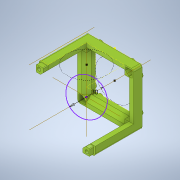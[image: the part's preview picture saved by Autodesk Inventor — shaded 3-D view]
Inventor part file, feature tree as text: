
AUTODESK INVENTOR PART (.ipt)
format: ipt  version: 2022 (Build 260153000, 153)  size: 558,080 bytes
history: native  units: mm
features: projected_geometry x16, sketch x13, extrude x11, plane x7, other x5, hole x3, fillet x2
ambient origin geometry x8: Origin, YZ Plane, XZ Plane, XY Plane, X Axis, Y Axis, Z Axis, Center Point
bodies: Solid1 (feature_tree)
feature tree (57):
  extrude  "Extrusion1"  Depth=49.7mm
  extrude  "Extrusion2"  Depth=8.0mm TaperAngle=0.0deg
  hole  "Hole1"  [1 undecoded]
  sketch  "Sketch4"  dims[d8=3.1mm d9=6.0mm d10=5.5mm d11=4.6mm d12=90.0deg d13=16.0mm d14=20.594885mm d23=2.0mm d30=33.8mm d31=0.0mm]
  sketch  "Sketch5"  dims[d35=33.8mm d36=0.0mm d39=53.8mm]
  other  "Work Axis1"
  other  "Work Axis2"
  fillet  "Fillet1"  Radius=33.8mm
  extrude  "Extrusion3"  Depth=53.8mm
  extrude  "Extrusion4"  Depth=2.0mm
  plane  "Work Plane1"
  extrude  "Extrusion5"  Depth=3.65mm
  hole  "Hole2"  [1 undecoded]
  extrude  "Extrusion6"  Depth=3.65mm
  extrude  "Extrusion7"  Depth=3.78mm
  extrude  "Extrusion8"  Depth=3.78mm
  fillet  "Fillet2"  Radius=3.78mm
  extrude  "Extrusion9"  Depth=10.0mm TaperAngle=0.0deg
  extrude  "Extrusion10"  Depth=3.7mm TaperAngle=0.0deg
  plane  "Work Plane2"
  plane  "Work Plane3"
  hole  "Hole9"  [1 undecoded]
  extrude  "Extrusion11"  Depth=2.0mm
  other  "Work Axis18"
  plane  "Work Plane4"
  sketch  "Sketch23"  dims[d112=45.0deg d120=10.0mm d121=0.0mm d124=3.7mm d125=0.0mm d130=4.2mm d131=0.0mm d132=2.0mm d133=0.5mm d134=3.4mm d135=21.0mm d136=7.38mm d137=3.69mm d138=40.0mm d140=360.0deg d142=4.0mm d143=0.0mm d144=4.95mm d145=2.05mm d146=5.5mm d147=40.0mm d149=360.0deg d151=2.2mm d152=0.0mm d153=3.1mm d154=6.0mm d155=5.5mm d156=3.2mm d157=90.0deg d158=16.0mm d159=20.594885mm d160=5.5mm d161=90.0deg d162=10.0mm d163=0.0mm d164=3.1mm d169=6.1mm d170=6.1mm d171=6.1mm d172=6.1mm d173=1.1mm d174=1.1mm d175=3.78mm d176=3.78mm d177=4.18mm d178=4.18mm d179=4.18mm d180=4.18mm d181=4.18mm d182=4.18mm d183=4.18mm d184=30.0mm d185=0.2mm d186=0.2mm]
  other  "Work Axis19"
  plane  "Arbeitsebene7"
  sketch  "Sketch1"  dims[d0=49.7mm d1=49.7mm]
  sketch  "Sketch2"  dims[d2=7.88mm d3=8.0mm d4=0.0mm]
  projected_geometry  "Projected Loop1"
  sketch  "Sketch3"  dims[d5=34.1mm d6=0.0mm]
  projected_geometry  "Projected Loop3"
  projected_geometry  "Projected Loop4"
  projected_geometry  "Projected Loop5"
  projected_geometry  "Projected Loop6"
  projected_geometry  "Projected Loop7"
  sketch  "Sketch9"  dims[d40=33.8mm d41=0.0mm]
  sketch  "Sketch16"  dims[d42=2.8mm d43=6.0mm d44=3.0mm d45=2.0mm d46=90.0deg d47=12.0mm d48=20.594885mm d96=3.65mm]
  projected_geometry  "Projected Loop14"
  projected_geometry  "Projected Loop15"
  projected_geometry  "Projected Loop16"
  projected_geometry  "Projected Loop17"
  sketch  "Sketch18"  dims[d97=3.65mm d98=3.65mm]
  sketch  "Sketch19"  dims[d99=3.65mm d100=3.65mm]
  projected_geometry  "Projected Loop22"
  sketch  "Sketch20"  dims[d101=3.65mm d102=3.65mm]
  projected_geometry  "Projected Loop23"
  sketch  "Sketch21"  dims[d105=3.78mm d106=3.78mm]
  projected_geometry  "Projected Loop24"
  sketch  "Sketch22"  dims[d107=3.78mm d109=3.78mm d110=3.78mm]
  projected_geometry  "Projected Loop25"
  projected_geometry  "Projected Loop28"
  projected_geometry  "Projected Loop29"
  other  "Work Point1"
  plane  "Work Plane5"
  plane  "Work Plane6"
note: 3 required parameter values undecoded (feature->parameter linkage not recoverable at this tier; creation-order binding heuristic only, values carry confidence <= 0.55)
